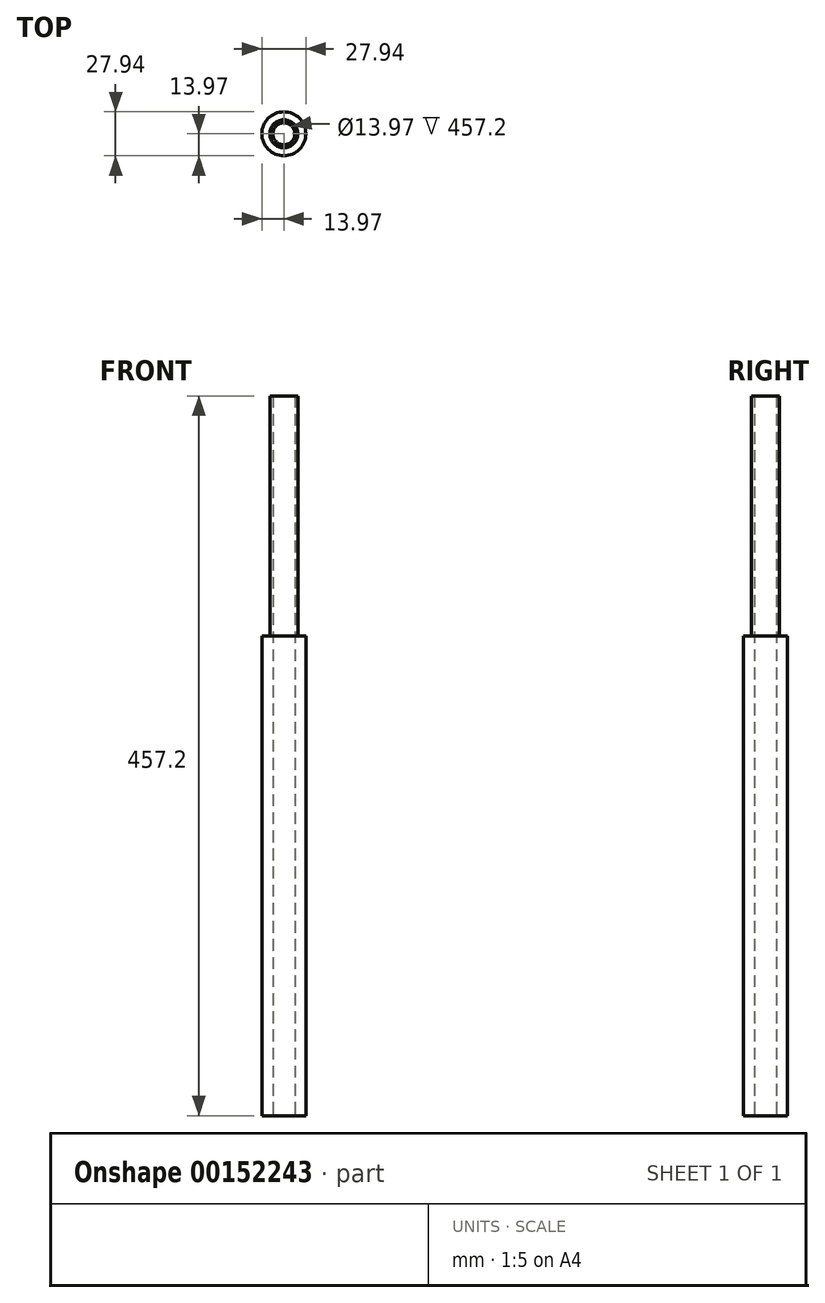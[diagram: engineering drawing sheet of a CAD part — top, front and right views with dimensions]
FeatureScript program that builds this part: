
annotation { "Feature Type Name" : "Feature", "Feature Type Description" : "" }
export const myFeature = defineFeature(function(context is Context, id is Id, definition is map)
    precondition{}
    {
        {
            var Q0;
            Q0=qCreatedBy(makeId("Front.planeOp"),FACE);
            var sketch = newSketch(context, id + "F0", { "sketchPlane" : qUnion([Q0])});
            skLineSegment(sketch, "E0", {"start": v(-51.39, 0) * mm, "end": v(47.88, 0) * mm, "construction": true});
            skLineSegment(sketch, "E1", {"start": v(0, -40.73) * mm, "end": v(0, 60.3) * mm, "construction": true});
            skLineSegment(sketch, "E2", {"start": v(0, 0) * mm, "end": v(0, 304.8) * mm});
            skLineSegment(sketch, "E3", {"start": v(0, 304.8) * mm, "end": v(13.97, 304.8) * mm});
            skLineSegment(sketch, "E4", {"start": v(13.97, 304.8) * mm, "end": v(13.97, 0) * mm});
            skLineSegment(sketch, "E5", {"start": v(13.97, 0) * mm, "end": v(0, 0) * mm});
            skLineSegment(sketch, "E6", {"start": v(0, 304.8) * mm, "end": v(0, 457.2) * mm});
            skLineSegment(sketch, "E7", {"start": v(0, 457.2) * mm, "end": v(8.9, 457.2) * mm});
            skLineSegment(sketch, "E8", {"start": v(8.9, 457.2) * mm, "end": v(8.9, 304.8) * mm});
            skLineSegment(sketch, "E9", {"start": v(8.9, 304.8) * mm, "end": v(0, 304.8) * mm});
            skSolve(sketch);
        }
        {
            var Q0;
            Q0=makeQuery(id+"F0.imprint","IMPRINT",FACE,{"disambiguationData":[TD([[makeQuery(id+"F0.imprint","IMPRINT",EDGE,{"derivedFrom":sQuery(id+"F0.wireOp",EDGE,"E2")}),-1.0]])]});
            var Q1;
            Q1=makeQuery(id+"F0.imprint","IMPRINT",FACE,{"disambiguationData":[TD([[makeQuery(id+"F0.imprint","IMPRINT",EDGE,{"derivedFrom":sQuery(id+"F0.wireOp",EDGE,"E6")}),-1.0]])]});
            var Q2;
            Q2=sQuery(id+"F0.wireOp",EDGE,"E2");
            revolve(context, id + "F1", {"entities" : qUnion([Q0, Q1]), "axis" : qUnion([Q2]), "revolveType" : RevolveType.FULL});
        }
        {
            var Q0;
            Q0=qCreatedBy(makeId("Top.planeOp"),FACE);
            var sketch = newSketch(context, id + "F2", { "sketchPlane" : qUnion([Q0])});
            skCircle(sketch, "E10", {"center": v(0, 0) * mm, "radius": 6.99 * mm});
            skSolve(sketch);
        }
        {
            var Q0;
            Q0 = qSketchRegion(id + "F2", true);
            extrude(context, id + "F3", {"entities" : qUnion([Q0]), "operationType" : NewBodyOperationType.REMOVE, "endBound" : BoundingType.THROUGH_ALL, "depth" : 25.4 * mm});
        }
    });
